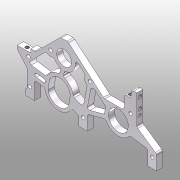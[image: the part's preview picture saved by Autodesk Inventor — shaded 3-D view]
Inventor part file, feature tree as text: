
AUTODESK INVENTOR PART (.ipt)
format: ipt  version: 2016 (Build 200138000, 138)  size: 419,328 bytes
history: native  units: mm
features: sketch x26, extrude x9, hole x9, thread x7, fillet x2, plane x1
ambient origin geometry x8: Origin, YZ Plane, XZ Plane, XY Plane, X Axis, Y Axis, Z Axis, Center Point
bodies: Solid1 (feature_tree)
feature tree (54):
  plane  "Work Plane1"
  extrude  "Extrude8"  Depth=5.0mm
  fillet  "Fillet1"  Radius=2.0mm
  extrude  "Extrude7"  Depth=2.0mm
  extrude  "Extrude6"  Depth=2.0mm
  extrude  "Extrude5"  Depth=2.0mm
  extrude  "Extrude4"  Depth=2.0mm
  extrude  "Extrude3"  Depth=1.5mm
  extrude  "Extrude2"  Depth=1.5mm
  extrude  "Extrude1"  Depth=2.0mm
  hole  "Hole8"  [1 undecoded]
  hole  "Hole7"  [1 undecoded]
  hole  "Hole6"  [1 undecoded]
  hole  "Hole5"  [1 undecoded]
  hole  "Hole4"  [1 undecoded]
  hole  "Hole3"  [1 undecoded]
  hole  "Hole2"  [1 undecoded]
  hole  "Hole1"  [1 undecoded]
  thread  "Thread1"  [1 undecoded]
  thread  "Thread2"  [1 undecoded]
  thread  "Thread3"  [1 undecoded]
  thread  "Thread4"  [1 undecoded]
  thread  "Thread5"  [1 undecoded]
  thread  "Thread6"  [1 undecoded]
  thread  "Thread7"  [1 undecoded]
  hole  "Hole23"  [1 undecoded]
  extrude  "Extrusion11"  [1 undecoded]
  fillet  "Fillet2"  [1 undecoded]
  sketch  "Sketch25"  dims[d99=3.0mm d100=6.0mm d101=4.0mm d102=2.0mm d103=90.0deg d104=8.0mm d105=20.594885mm]
  sketch  "Sketch1"  dims[d0=21.5mm d1=5.0mm d2=0.0mm d3=2.0mm]
  sketch  "Sketch2"  dims[d4=2.0mm d5=2.0mm]
  sketch  "Sketch3"  dims[d6=2.0mm d7=2.0mm]
  sketch  "Sketch4"  dims[d8=2.0mm d9=2.0mm]
  sketch  "Sketch5"  dims[d10=2.0mm d11=2.0mm]
  sketch  "Sketch6"  dims[d12=1.5mm d13=1.5mm]
  sketch  "Sketch7"  dims[d14=1.5mm d15=1.5mm]
  sketch  "Sketch8"  dims[d16=2.0mm d17=2.0mm]
  sketch  "Sketch9"  dims[d18=2.0mm d19=2.0mm]
  sketch  "Sketch10"  dims[d20=2.0mm d21=2.0mm]
  sketch  "Sketch11"  dims[d22=3.0mm d23=-0.0mm d24=5.0mm d25=-0.0mm]
  sketch  "Sketch12"  dims[d26=5.0mm d27=-0.0mm d28=5.0mm d29=-0.0mm]
  sketch  "Sketch13"  dims[d30=5.0mm d31=-0.0mm d32=5.0mm d33=-0.0mm]
  sketch  "Sketch14"  dims[d34=5.0mm d35=-0.0mm]
  sketch  "Sketch15"  dims[d36=3.0mm d37=6.0mm d38=4.0mm d39=2.0mm d40=90.0deg d41=6.0mm d42=20.594885mm]
  sketch  "Sketch16"  dims[d43=3.0mm d44=6.0mm d45=4.0mm d46=2.0mm d47=90.0deg d48=4.0mm d49=20.594885mm]
  sketch  "Sketch17"  dims[d50=3.0mm d51=6.0mm d52=4.0mm d53=2.0mm d54=90.0deg d55=8.0mm d56=20.594885mm]
  sketch  "Sketch18"  dims[d57=3.0mm d58=6.0mm d59=4.0mm d60=2.0mm d61=90.0deg d62=8.0mm d63=20.594885mm]
  sketch  "Sketch19"  dims[d64=3.0mm d65=6.0mm d66=4.0mm d67=2.0mm d68=90.0deg d69=8.0mm d70=20.594885mm]
  sketch  "Sketch20"  dims[d71=3.0mm d72=6.0mm d73=4.0mm d74=2.0mm d75=90.0deg d76=8.0mm d77=20.594885mm]
  sketch  "Sketch21"  dims[d78=3.0mm d79=6.0mm d80=4.0mm d81=2.0mm d82=90.0deg d83=8.0mm d84=20.594885mm]
  sketch  "Sketch22"  dims[d85=3.0mm d86=6.0mm d87=4.0mm d88=2.0mm d89=90.0deg d90=8.0mm d91=20.594885mm]
  sketch  "Sketch23"  dims[d92=3.0mm d93=6.0mm d94=4.0mm d95=2.0mm d96=90.0deg d97=8.0mm d98=20.594885mm]
  sketch  "Sketch26"  dims[d106=12.0mm d107=6.0mm d108=4.0mm d109=2.0mm d110=90.0deg d111=8.0mm d112=20.594885mm]
  sketch  "Sketch27"  dims[d113=3.0mm d114=6.0mm d115=4.0mm d116=2.0mm d117=90.0deg d118=8.0mm d119=20.594885mm d120=3.0mm d121=6.0mm d122=4.0mm d123=2.0mm d124=90.0deg d125=5.0mm d126=0.0mm d127=3.0mm d128=4.0mm d129=4.0mm d130=2.0mm d131=90.0deg d132=5.0mm d133=0.0mm d134=3.0mm d135=6.0mm d136=4.0mm d137=2.0mm d138=90.0deg d139=5.0mm d140=0.0mm d145=3.0mm d146=4.0mm d151=10.0mm d152=0.0mm d153=10.0mm d154=0.0mm d155=10.0mm d156=0.0mm d157=10.0mm d158=0.0mm d159=10.0mm d160=0.0mm d161=10.0mm d162=0.0mm d163=10.0mm d164=0.0mm d165=17.0mm d166=2.459mm d167=6.0mm d168=4.0mm d169=2.0mm d170=90.0deg d171=2.75mm d172=20.594885mm d173=1.0mm d174=0.0mm d175=2.0mm]
note: 18 required parameter values undecoded (feature->parameter linkage not recoverable at this tier; creation-order binding heuristic only, values carry confidence <= 0.55)
